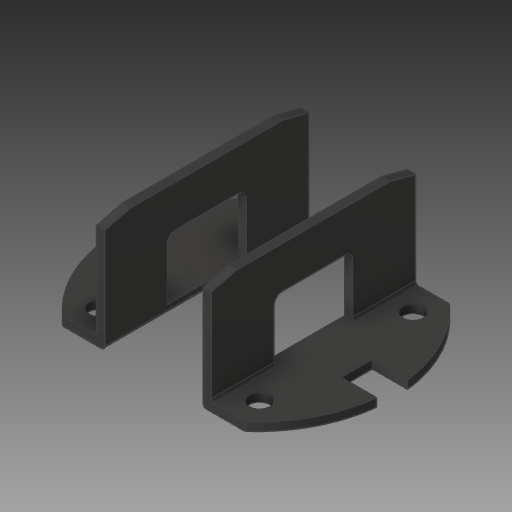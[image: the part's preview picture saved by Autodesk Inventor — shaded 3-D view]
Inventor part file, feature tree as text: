
AUTODESK INVENTOR PART (.ipt)
format: ipt  version: 2018 (Build 220112000, 112)  size: 141,824 bytes
history: native  units: mm
features: other x2, fillet x2
ambient origin geometry x8: Origin, YZ Plane, XZ Plane, XY Plane, X Axis, Y Axis, Z Axis, Center Point
bodies: Body1 (feature_tree), Body2 (feature_tree)
feature tree (4):
  other  "ソリッド1"
  other  "ソリッド2"
  fillet  "Fillet1"  [1 undecoded]
  fillet  "Fillet2"  [1 undecoded]
note: 2 required parameter values undecoded (feature->parameter linkage not recoverable at this tier; creation-order binding heuristic only, values carry confidence <= 0.55)
